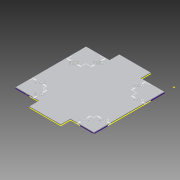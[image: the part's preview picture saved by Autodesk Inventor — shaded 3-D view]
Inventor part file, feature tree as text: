
AUTODESK INVENTOR PART (.ipt)
format: ipt  version: 2014 SP1 (Build 180222100, 222)  size: 126,464 bytes
history: native  units: in
note: dims shown in document units (in); Inventor stores cm internally (conversion verified against a paired STEP export)
features: extrude x3, sketch x3
ambient origin geometry x8: Origin, YZ Plane, XZ Plane, XY Plane, X Axis, Y Axis, Z Axis, Center Point
bodies: Solid1 (feature_tree)
feature tree (6):
  extrude  "Extrusion1"  Depth=23.0in
  extrude  "Extrusion2"  Depth=6.0in
  extrude  "Extrusion4"  Depth=6.0in
  sketch  "Sketch1"  dims[d0=20.0in d1=23.0in]
  sketch  "Sketch2"  dims[d2=0.25in d3=0.0in d4=6.0in]
  sketch  "Sketch5"  dims[d5=2.5in d6=6.0in d7=2.5in d8=6.0in d9=2.5in d10=6.0in d11=2.5in d12=1.0in d13=0.0in d24=3.5in d25=3.5in d26=3.5in d27=3.5in d28=3.5in d29=3.5in d30=3.5in d31=3.5in d32=0.25in d33=0.0in]
